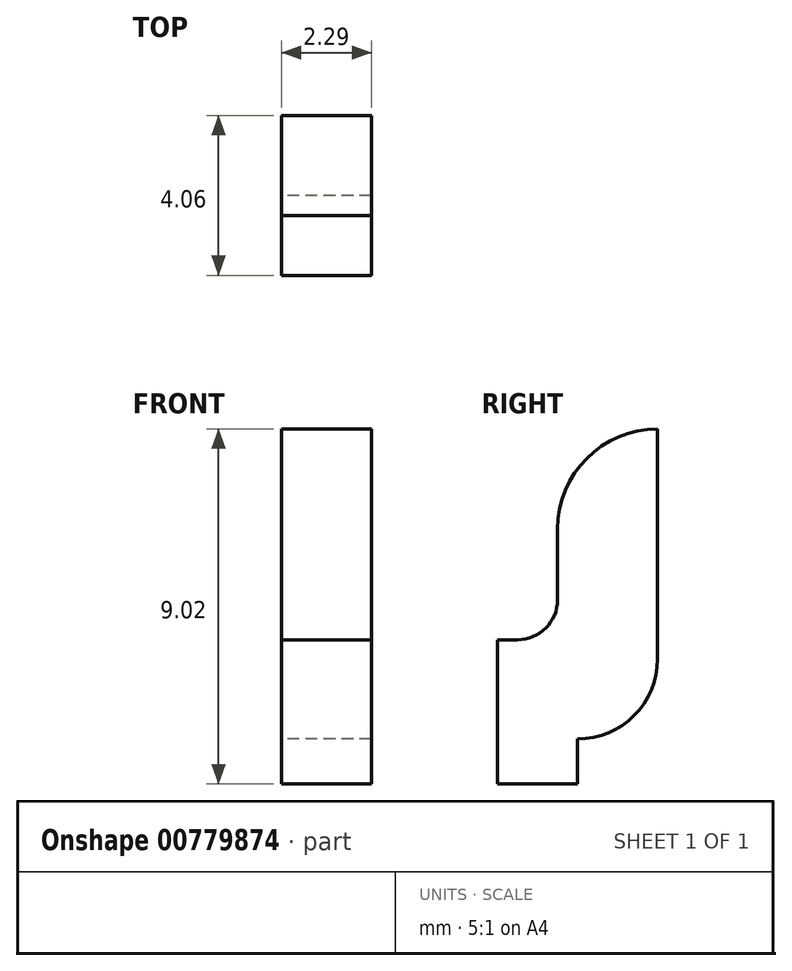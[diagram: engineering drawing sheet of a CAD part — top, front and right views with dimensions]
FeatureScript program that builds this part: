
annotation { "Feature Type Name" : "Feature", "Feature Type Description" : "" }
export const myFeature = defineFeature(function(context is Context, id is Id, definition is map)
    precondition{}
    {
        {
            var Q0;
            Q0=qCreatedBy(makeId("Right.planeOp"),FACE);
            var sketch = newSketch(context, id + "F0", { "sketchPlane" : qUnion([Q0])});
            skLineSegment(sketch, "E0", {"start": v(19.74, 49.03) * mm, "end": v(15.35, 49.03) * mm});
            skLineSegment(sketch, "E1", {"start": v(15.35, 49.03) * mm, "end": v(0, 40) * mm});
            skLineSegment(sketch, "E2", {"start": v(0, 40) * mm, "end": v(0, 33.2) * mm});
            skLineSegment(sketch, "E3", {"start": v(0, 33.2) * mm, "end": v(5.87, 33.2) * mm});
            skLineSegment(sketch, "E4", {"start": v(19.74, 49.03) * mm, "end": v(19.74, 42.68) * mm});
            skFitSpline(sketch, "E5", {"points": [v(5.87, 33.2) * mm, v(13.58, 33.2) * mm, v(18.07, 39.32) * mm, v(19.74, 42.68) * mm], "startDerivative": vector(44.3, 0) * mm, "endDerivative": vector(-0.6, 37.62) * mm});
            skFitSpline(sketch, "E6", {"points": [v(19.74, 49.03) * mm, v(18.3, 48.12) * mm, v(17.12, 46.54) * mm, v(16.64, 42.89) * mm, v(16.16, 40.82) * mm, v(23.7, 41.71) * mm], "startDerivative": vector(-9.89, -5.63) * mm, "endDerivative": vector(33.59, 7.6) * mm});
            skLineSegment(sketch, "E7", {"start": v(31.48, 37.53) * mm, "end": v(31.48, 31.68) * mm});
            skLineSegment(sketch, "E8", {"start": v(27.42, 29.9) * mm, "end": v(27.42, 32.17) * mm});
            skLineSegment(sketch, "E9", {"start": v(27.42, 32.17) * mm, "end": v(28.94, 32.17) * mm});
            skLineSegment(sketch, "E10", {"start": v(28.94, 32.17) * mm, "end": v(28.94, 34.99) * mm});
            skLineSegment(sketch, "E11", {"start": v(31.48, 37.53) * mm, "end": v(31.48, 37.53) * mm});
            skPoint(sketch, "E12.visualSharp", {"position": v(31.48, 29.9) * mm});
            skArc(sketch, "E12.filletArc", {"start": v(29.45, 29.65) * mm, "mid": v(30.89, 30.25) * mm, "end": v(31.48, 31.68) * mm});
            skLineSegment(sketch, "E13", {"start": v(29.45, 29.65) * mm, "end": v(29.45, 28.5) * mm});
            skLineSegment(sketch, "E14", {"start": v(29.45, 28.5) * mm, "end": v(27.42, 28.5) * mm});
            skLineSegment(sketch, "E15", {"start": v(27.42, 28.5) * mm, "end": v(27.42, 29.9) * mm});
            skPoint(sketch, "E16.visualSharp", {"position": v(28.94, 37.53) * mm});
            skArc(sketch, "E16.filletArc", {"start": v(31.48, 37.53) * mm, "mid": v(29.69, 36.78) * mm, "end": v(28.94, 34.99) * mm});
            skSolve(sketch);
        }
        {
            var Q0;
            Q0=makeQuery(id+"F0.imprint","IMPRINT",FACE,{"disambiguationData":[TD([[makeQuery(id+"F0.imprint","IMPRINT",EDGE,{"derivedFrom":sQuery(id+"F0.wireOp",EDGE,"E7")}),-1.0]])]});
            extrude(context, id + "F1", {"entities" : qUnion([Q0]), "depth" : 2.3 * mm, "offsetDistance" : 25.4 * mm});
        }
        {
            var Q0;
            Q0=makeQuery(id+"F1.opExtrude","SWEPT_EDGE",EDGE,{"disambiguationData":[OSD([sQuery(id+"F0.wireOp",EDGE,"E9"),sQuery(id+"F0.wireOp",EDGE,"E10")])]});
            fillet(context, id + "F2", {"entities" : qUnion([Q0]), "radius" : 1.02 * mm, "tangentPropagation" : true, "allowEdgeOverflow" : false});
        }
    });
